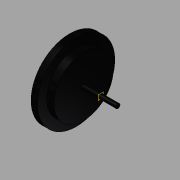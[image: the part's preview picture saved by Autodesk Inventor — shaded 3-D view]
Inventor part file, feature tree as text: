
AUTODESK INVENTOR PART (.ipt)
format: ipt  version: 2015 (Build 190159000, 159)  size: 141,312 bytes
history: native  units: in
note: dims shown in document units (in); Inventor stores cm internally (conversion verified against a paired STEP export)
features: sketch x5, other x3, plane x1
ambient origin geometry x8: Origin, YZ Plane, XZ Plane, XY Plane, X Axis, Y Axis, Z Axis, Center Point
bodies: Solid1 (feature_tree)
feature tree (9):
  other  "rueda_MIR2.ipt"
  other  "Solid1::rueda_MIR2.ipt"
  other  "TaggingFeature1"
  sketch  "Sketch2"  dims[d0=0.3937in]
  sketch  "Sketch3"
  sketch  "Sketch7"
  sketch  "Sketch12"
  sketch  "Sketch13"
  plane  "Work Plane1"
